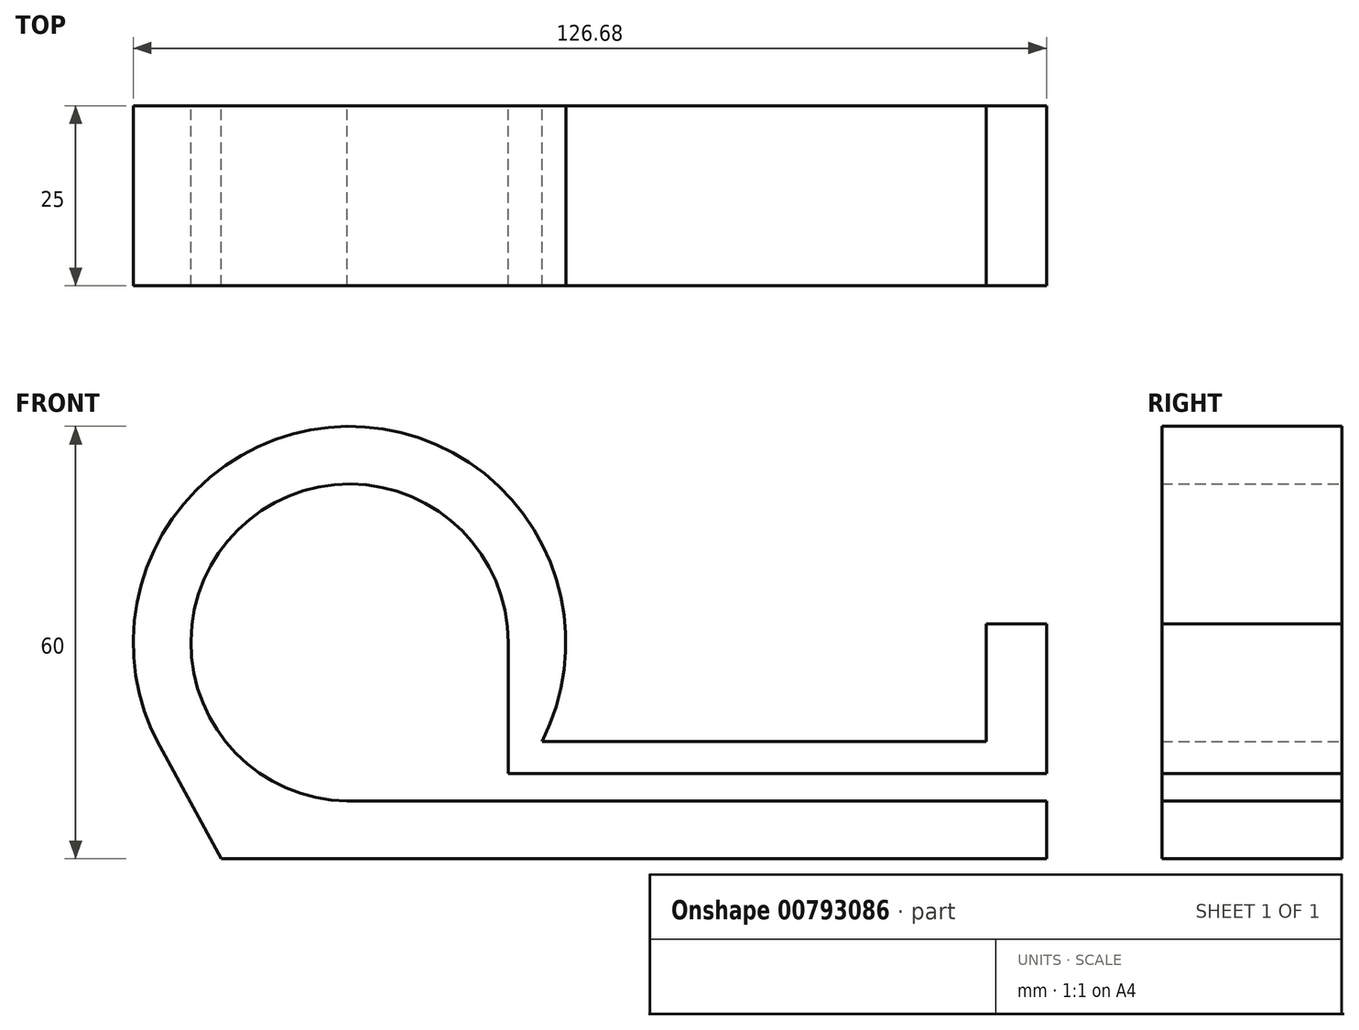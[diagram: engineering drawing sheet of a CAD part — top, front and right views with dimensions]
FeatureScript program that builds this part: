
annotation { "Feature Type Name" : "Feature", "Feature Type Description" : "" }
export const myFeature = defineFeature(function(context is Context, id is Id, definition is map)
    precondition{}
    {
        {
            var Q0;
            Q0=qCreatedBy(makeId("Front.planeOp"),FACE);
            var sketch = newSketch(context, id + "F0", { "sketchPlane" : qUnion([Q0])});
            skArc(sketch, "E0", {"start": v(-9.69, 20.42) * mm, "mid": v(-36.77, 64.1) * mm, "end": v(-62.71, 19.73) * mm});
            skArc(sketch, "E1", {"start": v(-14.38, 34.11) * mm, "mid": v(-52.05, 49.56) * mm, "end": v(-36.08, 12.11) * mm});
            skLineSegment(sketch, "E2", {"start": v(-63.32, 20.84) * mm, "end": v(-54.18, 4.11) * mm});
            skLineSegment(sketch, "E3", {"start": v(-54.18, 4.11) * mm, "end": v(60.3, 4.11) * mm});
            skLineSegment(sketch, "E4", {"start": v(-36.38, 34.11) * mm, "end": v(46.8, 56.4) * mm, "construction": true});
            skLineSegment(sketch, "E5", {"start": v(-36.38, 34.11) * mm, "end": v(45.04, 34.11) * mm, "construction": true});
            skLineSegment(sketch, "E6", {"start": v(-9.69, 20.42) * mm, "end": v(51.95, 20.42) * mm});
            skLineSegment(sketch, "E7", {"start": v(60.3, 20.42) * mm, "end": v(60.3, 15.97) * mm});
            skLineSegment(sketch, "E8", {"start": v(60.3, 20.42) * mm, "end": v(60.3, 36.7) * mm});
            skLineSegment(sketch, "E9", {"start": v(51.95, 36.7) * mm, "end": v(51.95, 20.42) * mm});
            skLineSegment(sketch, "E10", {"start": v(51.95, 36.7) * mm, "end": v(60.3, 36.7) * mm});
            skLineSegment(sketch, "E11", {"start": v(-36.69, 12.11) * mm, "end": v(60.3, 12.11) * mm});
            skLineSegment(sketch, "E12", {"start": v(-14.38, 34.11) * mm, "end": v(-14.38, 15.97) * mm});
            skLineSegment(sketch, "E13", {"start": v(-14.38, 15.97) * mm, "end": v(60.3, 15.97) * mm});
            skLineSegment(sketch, "E14.trimOffspring", {"start": v(60.3, 12.11) * mm, "end": v(60.3, 4.11) * mm});
            skSolve(sketch);
        }
        {
            var Q0;
            Q0 = qSketchRegion(id + "F0", true);
            extrude(context, id + "F1", {"entities" : qUnion([Q0]), "depth" : 25 * mm, "offsetDistance" : 25 * mm});
        }
    });
